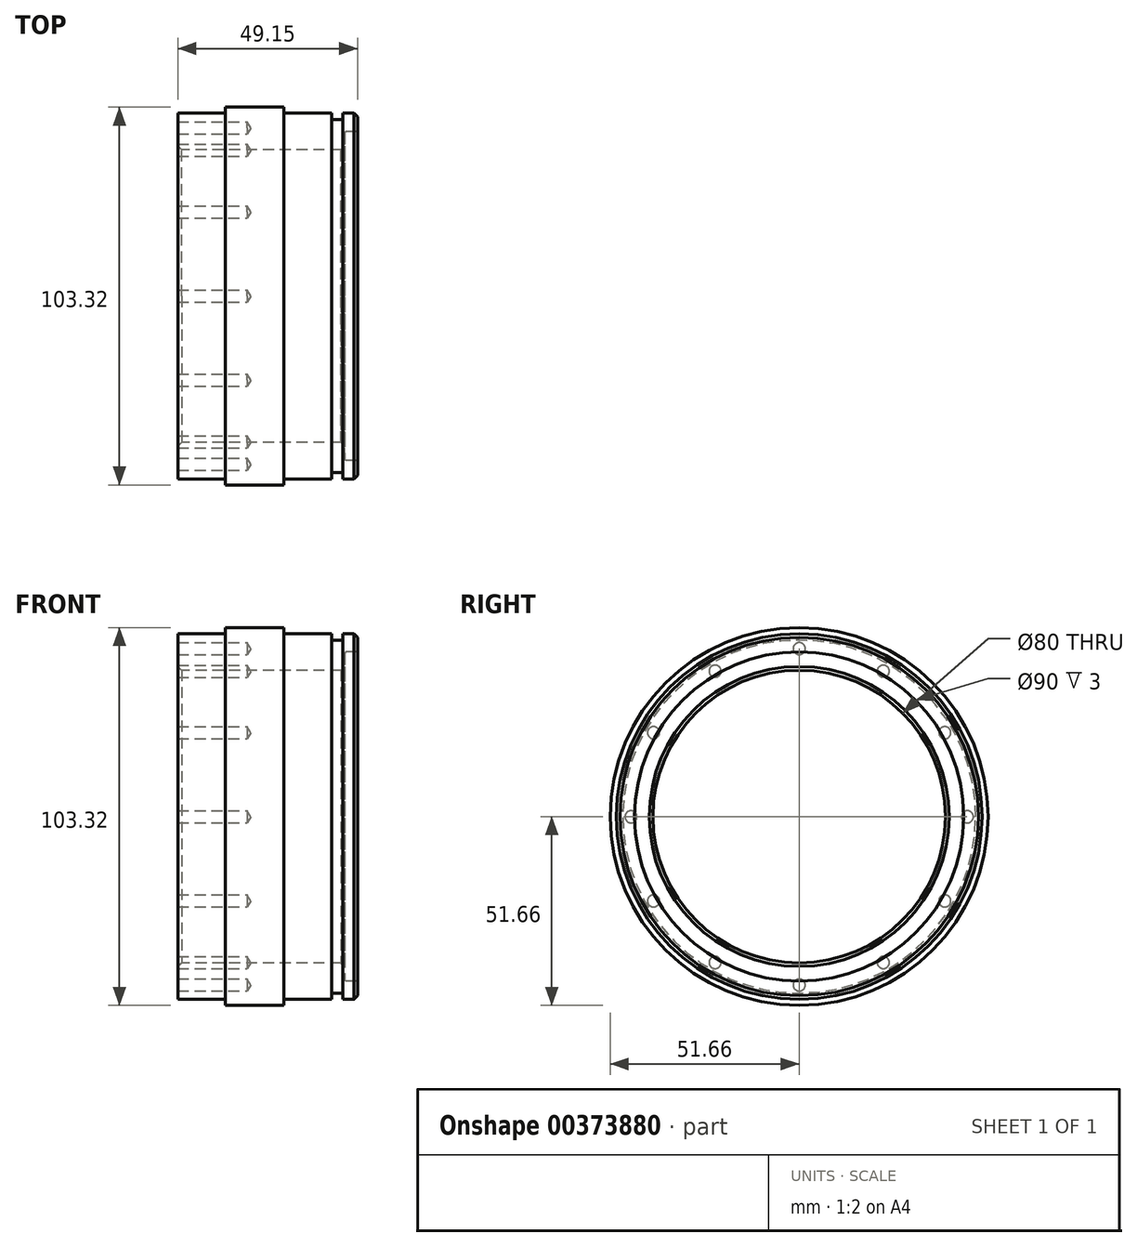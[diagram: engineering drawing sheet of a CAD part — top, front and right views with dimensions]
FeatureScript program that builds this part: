
annotation { "Feature Type Name" : "Feature", "Feature Type Description" : "" }
export const myFeature = defineFeature(function(context is Context, id is Id, definition is map)
    precondition{}
    {
        {
            var Q0;
            Q0=qCreatedBy(makeId("Front.planeOp"),FACE);
            var sketch = newSketch(context, id + "F0", { "sketchPlane" : qUnion([Q0])});
            skLineSegment(sketch, "E0", {"start": v(-26.06, -44.48) * mm, "end": v(52.5, -44.48) * mm, "construction": true});
            skLineSegment(sketch, "E1", {"start": v(-30.1, 5.52) * mm, "end": v(-30.1, -4.48) * mm});
            skLineSegment(sketch, "E2", {"start": v(-30.1, 5.52) * mm, "end": v(-17.6, 5.52) * mm});
            skLineSegment(sketch, "E3", {"start": v(-17.1, 6.02) * mm, "end": v(-17.1, 7.18) * mm});
            skLineSegment(sketch, "E4", {"start": v(-17.1, 7.18) * mm, "end": v(-1.1, 7.18) * mm});
            skLineSegment(sketch, "E5", {"start": v(-1.1, 7.18) * mm, "end": v(-1.1, 6.02) * mm});
            skLineSegment(sketch, "E6", {"start": v(-0.6, 5.52) * mm, "end": v(11.9, 5.52) * mm});
            skLineSegment(sketch, "E7", {"start": v(11.9, 5.52) * mm, "end": v(11.9, 3.77) * mm});
            skLineSegment(sketch, "E8", {"start": v(11.9, 3.77) * mm, "end": v(15.05, 3.77) * mm});
            skLineSegment(sketch, "E9", {"start": v(15.05, 3.77) * mm, "end": v(15.05, 5.52) * mm});
            skLineSegment(sketch, "E10", {"start": v(15.05, 5.52) * mm, "end": v(19.05, 5.52) * mm});
            skLineSegment(sketch, "E11", {"start": v(19.05, 5.52) * mm, "end": v(19.05, 0.52) * mm});
            skLineSegment(sketch, "E12", {"start": v(15.55, -4.48) * mm, "end": v(-30.1, -4.48) * mm});
            skLineSegment(sketch, "E13.top", {"start": v(19.05, 0.52) * mm, "end": v(16.05, 0.52) * mm});
            skLineSegment(sketch, "E13.right", {"start": v(15.55, -4.48) * mm, "end": v(15.55, 0.02) * mm});
            skPoint(sketch, "E14.visualSharp", {"position": v(15.55, 0.52) * mm});
            skArc(sketch, "E14.filletArc", {"start": v(16.05, 0.52) * mm, "mid": v(15.7, 0.37) * mm, "end": v(15.55, 0.02) * mm});
            skPoint(sketch, "E15.visualSharp", {"position": v(-1.1, 5.52) * mm});
            skArc(sketch, "E15.filletArc", {"start": v(-1.1, 6.02) * mm, "mid": v(-0.95, 5.66) * mm, "end": v(-0.6, 5.52) * mm});
            skPoint(sketch, "E16.visualSharp", {"position": v(-17.1, 5.52) * mm});
            skArc(sketch, "E16.filletArc", {"start": v(-17.6, 5.52) * mm, "mid": v(-17.24, 5.66) * mm, "end": v(-17.1, 6.02) * mm});
            skSolve(sketch);
        }
        {
            var Q0;
            Q0 = qSketchRegion(id + "F0", true);
            var Q1;
            Q1=sQuery(id+"F0.wireOp",EDGE,"E0");
            revolve(context, id + "F1", {"entities" : qUnion([Q0]), "axis" : qUnion([Q1]), "revolveType" : RevolveType.FULL});
        }
        {
            var Q0;
            Q0=makeQuery(id+"F1.opRevolve","SWEPT_BODY",BODY,{"disambiguationData":[OSD([sQuery(id+"F0.wireOp",EDGE,"E1"),sQuery(id+"F0.wireOp",EDGE,"E2"),sQuery(id+"F0.wireOp",EDGE,"E3"),sQuery(id+"F0.wireOp",EDGE,"E4"),sQuery(id+"F0.wireOp",EDGE,"E5"),sQuery(id+"F0.wireOp",EDGE,"E6"),sQuery(id+"F0.wireOp",EDGE,"E7"),sQuery(id+"F0.wireOp",EDGE,"E8"),sQuery(id+"F0.wireOp",EDGE,"E9"),sQuery(id+"F0.wireOp",EDGE,"E10"),sQuery(id+"F0.wireOp",EDGE,"E11"),sQuery(id+"F0.wireOp",EDGE,"E12")])]});
            transform(context, id + "F2", {"entities" : qUnion([Q0]), "transformType" : TransformType.TRANSLATION_3D, "dx" : 0 * mm, "dy" : 0 * mm, "dz" : 44.56 * mm, "makeCopy" : false});
        }
        {
            var Q0;
            Q0=makeQuery(id+"F1.opRevolve","SWEPT_FACE",FACE,{"disambiguationData":[OSD([sQuery(id+"F0.wireOp",EDGE,"E1")])]});
            var sketch = newSketch(context, id + "F3", { "sketchPlane" : qUnion([Q0])});
            skLineSegment(sketch, "E17", {"start": v(0, 0) * mm, "end": v(0, 46) * mm, "construction": true});
            skPoint(sketch, "E18", {"position": v(0, 46) * mm});
            skPoint(sketch, "E19.1.0", {"position": v(-23, 39.84) * mm});
            skPoint(sketch, "E19.2.0", {"position": v(-39.84, 23) * mm});
            skPoint(sketch, "E19.3.0", {"position": v(-46, 0) * mm});
            skPoint(sketch, "E19.4.0", {"position": v(-39.84, -23) * mm});
            skPoint(sketch, "E19.5.0", {"position": v(-23, -39.84) * mm});
            skPoint(sketch, "E19.6.0", {"position": v(0, -46) * mm});
            skPoint(sketch, "E19.7.0", {"position": v(23, -39.84) * mm});
            skPoint(sketch, "E19.8.0", {"position": v(39.84, -23) * mm});
            skPoint(sketch, "E19.9.0", {"position": v(46, 0) * mm});
            skPoint(sketch, "E19.10.0", {"position": v(39.84, 23) * mm});
            skPoint(sketch, "E19.11.0", {"position": v(23, 39.84) * mm});
            skPoint(sketch, "E19.center", {"position": v(0, 0) * mm});
            skSolve(sketch);
        }
        {
            var Q0;
            Q0=sQuery(id+"F3.wireOp",VERTEX,"E18");
            var Q1;
            Q1=sQuery(id+"F3.wireOp",VERTEX,"E19.11.0");
            var Q2;
            Q2=sQuery(id+"F3.wireOp",VERTEX,"E19.10.0");
            var Q3;
            Q3=sQuery(id+"F3.wireOp",VERTEX,"E19.9.0");
            var Q4;
            Q4=sQuery(id+"F3.wireOp",VERTEX,"E19.8.0");
            var Q5;
            Q5=sQuery(id+"F3.wireOp",VERTEX,"E19.7.0");
            var Q6;
            Q6=sQuery(id+"F3.wireOp",VERTEX,"E19.6.0");
            var Q7;
            Q7=sQuery(id+"F3.wireOp",VERTEX,"E19.5.0");
            var Q8;
            Q8=sQuery(id+"F3.wireOp",VERTEX,"E19.4.0");
            var Q9;
            Q9=sQuery(id+"F3.wireOp",VERTEX,"E19.3.0");
            var Q10;
            Q10=sQuery(id+"F3.wireOp",VERTEX,"E19.2.0");
            var Q11;
            Q11=sQuery(id+"F3.wireOp",VERTEX,"E19.1.0");
            var Q12;
            Q12=makeQuery(id+"F1.opRevolve","SWEPT_BODY",BODY,{"disambiguationData":[OSD([sQuery(id+"F0.wireOp",EDGE,"E1"),sQuery(id+"F0.wireOp",EDGE,"E2"),sQuery(id+"F0.wireOp",EDGE,"E3"),sQuery(id+"F0.wireOp",EDGE,"E4"),sQuery(id+"F0.wireOp",EDGE,"E5"),sQuery(id+"F0.wireOp",EDGE,"E6"),sQuery(id+"F0.wireOp",EDGE,"E7"),sQuery(id+"F0.wireOp",EDGE,"E8"),sQuery(id+"F0.wireOp",EDGE,"E9"),sQuery(id+"F0.wireOp",EDGE,"E10"),sQuery(id+"F0.wireOp",EDGE,"E11"),sQuery(id+"F0.wireOp",EDGE,"E12")])]});
            hole(context, id + "F4", {"style" : HoleStyle.SIMPLE, "endStyle" : HoleEndStyle.BLIND, "standardTappedOrClearance" : lookupTablePath({ "standard" : "ISO", "engagement" : "75%", "pitch" : "0.7 mm", "size" : "M4", "type" : "Tapped" }), "standardBlindInLast" : lookupTablePath({ "standard" : "ISO", "engagement" : "75%", "pitch" : "0.7 mm", "size" : "M4", "type" : "Tapped" }), "holeDiameter" : 3.3 * mm, "showTappedDepth" : true, "holeDepth" : 18.93 * mm, "tappedDepth" : 16.82 * mm, "tapClearance" : 3, "locations" : qUnion([Q0, Q1, Q2, Q3, Q4, Q5, Q6, Q7, Q8, Q9, Q10, Q11]), "scope" : qUnion([Q12]), "majorDiameter" : 4 * mm, "startStyle" : HoleStartStyle.SKETCH});
        }
        {
            var Q0;
            Q0=makeQuery(id+"F1.opRevolve","SWEPT_FACE",FACE,{"disambiguationData":[OSD([sQuery(id+"F0.wireOp",EDGE,"E12")])]});
            var Q1;
            Q1=makeQuery(id+"F1.opRevolve","SWEPT_EDGE",EDGE,{"disambiguationData":[OSD([sQuery(id+"F0.wireOp",EDGE,"E10"),sQuery(id+"F0.wireOp",EDGE,"E11")])]});
            chamfer(context, id + "F5", {"entities" : qUnion([Q0, Q1]), "width" : 1 * mm, "tangentPropagation" : true});
        }
    });
